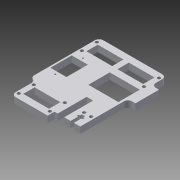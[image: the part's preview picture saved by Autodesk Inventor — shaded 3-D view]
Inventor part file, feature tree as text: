
AUTODESK INVENTOR PART (.ipt)
format: ipt  version: 2013 (Build 170138000, 138)  size: 156,672 bytes
history: native  units: mm
features: extrude x1, sketch x1
ambient origin geometry x8: Origin, YZ Plane, XZ Plane, XY Plane, X Axis, Y Axis, Z Axis, Center Point
bodies: Solid1 (feature_tree)
feature tree (2):
  extrude  "Extrusion1"  [1 undecoded]
  sketch  "Sketch1"  dims[d0=6.0mm d1=0.0mm]
note: 1 required parameter value undecoded (feature->parameter linkage not recoverable at this tier; creation-order binding heuristic only, values carry confidence <= 0.55)
